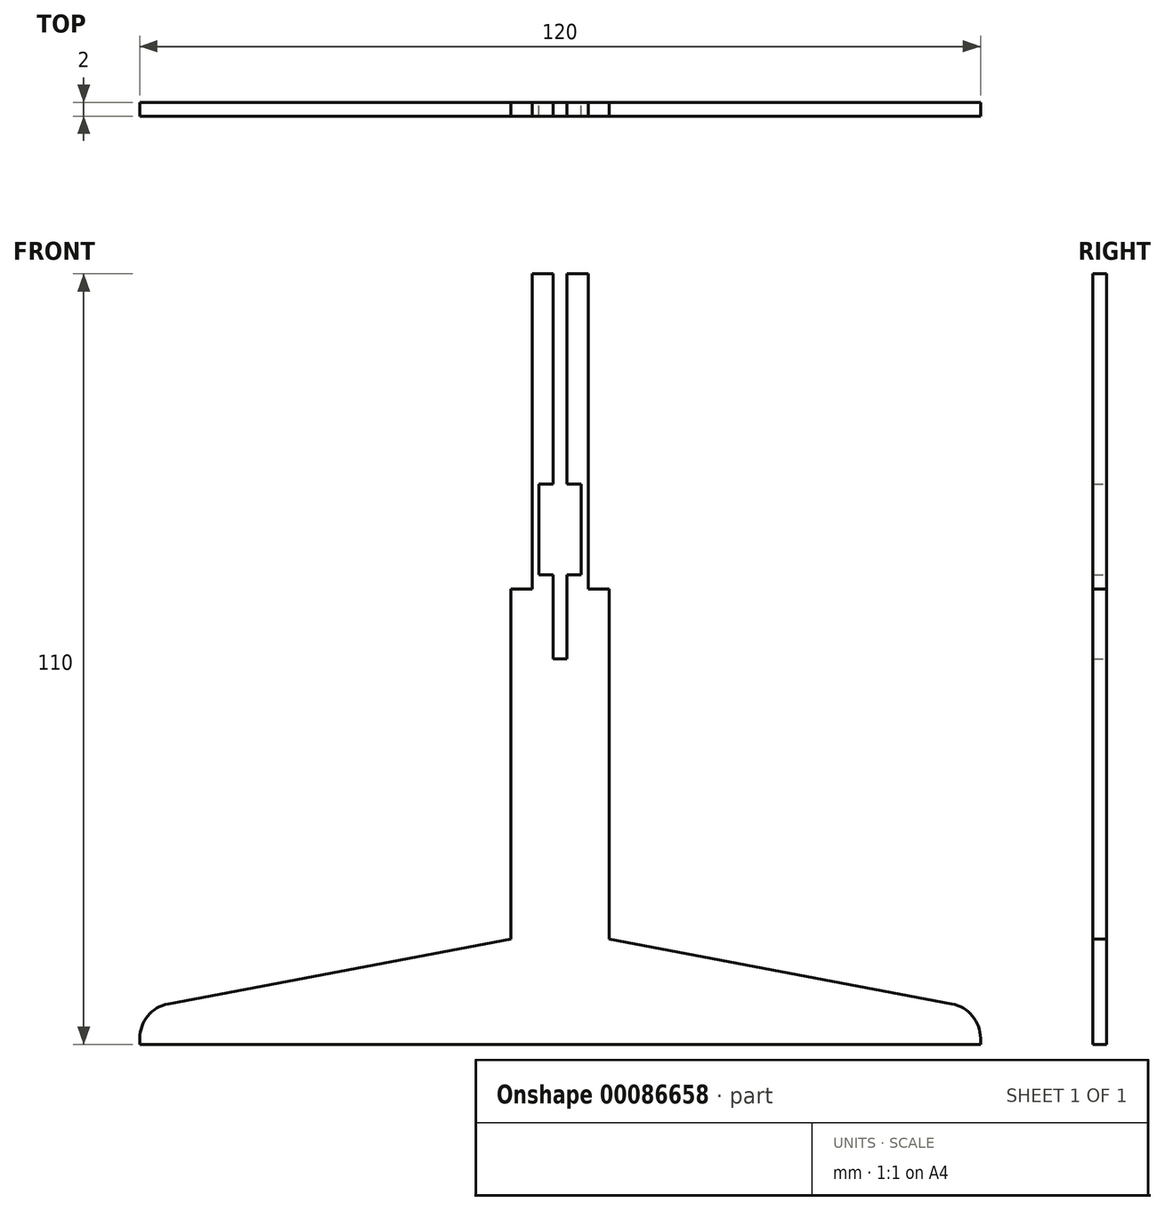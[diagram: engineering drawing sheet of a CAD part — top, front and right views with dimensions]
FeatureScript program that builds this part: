
annotation { "Feature Type Name" : "Feature", "Feature Type Description" : "" }
export const myFeature = defineFeature(function(context is Context, id is Id, definition is map)
    precondition{}
    {
        {
            var Q0;
            Q0=qCreatedBy(makeId("Front.planeOp"),FACE);
            var sketch = newSketch(context, id + "F0", { "sketchPlane" : qUnion([Q0])});
            skLineSegment(sketch, "E0", {"start": v(-1, 55) * mm, "end": v(1, 55) * mm});
            skLineSegment(sketch, "E1", {"start": v(1, 55) * mm, "end": v(1, 67) * mm});
            skLineSegment(sketch, "E2", {"start": v(1, 110) * mm, "end": v(4, 110) * mm});
            skLineSegment(sketch, "E3", {"start": v(4, 110) * mm, "end": v(4, 65) * mm});
            skLineSegment(sketch, "E4", {"start": v(4, 65) * mm, "end": v(7, 65) * mm});
            skLineSegment(sketch, "E5", {"start": v(7, 65) * mm, "end": v(7, 15) * mm});
            skLineSegment(sketch, "E6", {"start": v(60, 0) * mm, "end": v(-60, 0) * mm});
            skLineSegment(sketch, "E7", {"start": v(-7, 15) * mm, "end": v(-7, 65) * mm});
            skLineSegment(sketch, "E8", {"start": v(-7, 65) * mm, "end": v(-4, 65) * mm});
            skLineSegment(sketch, "E9", {"start": v(-4, 65) * mm, "end": v(-4, 110) * mm});
            skLineSegment(sketch, "E10", {"start": v(-4, 110) * mm, "end": v(-1, 110) * mm});
            skLineSegment(sketch, "E11", {"start": v(-1, 110) * mm, "end": v(-1, 80) * mm});
            skLineSegment(sketch, "E12", {"start": v(-1, 80) * mm, "end": v(-3, 80) * mm});
            skLineSegment(sketch, "E13", {"start": v(-3, 80) * mm, "end": v(-3, 67) * mm});
            skLineSegment(sketch, "E14", {"start": v(-3, 67) * mm, "end": v(-1, 67) * mm});
            skLineSegment(sketch, "E15", {"start": v(-1, 67) * mm, "end": v(-1, 55) * mm});
            skLineSegment(sketch, "E16", {"start": v(1, 67) * mm, "end": v(3, 67) * mm});
            skLineSegment(sketch, "E17", {"start": v(3, 67) * mm, "end": v(3, 80) * mm});
            skLineSegment(sketch, "E18", {"start": v(3, 80) * mm, "end": v(1, 80) * mm});
            skLineSegment(sketch, "E19", {"start": v(1, 80) * mm, "end": v(1, 110) * mm});
            skLineSegment(sketch, "E20", {"start": v(7, 15) * mm, "end": v(60, 5) * mm});
            skLineSegment(sketch, "E21", {"start": v(60, 5) * mm, "end": v(60, 0) * mm});
            skLineSegment(sketch, "E22", {"start": v(-7, 15) * mm, "end": v(-60, 5) * mm});
            skLineSegment(sketch, "E23", {"start": v(-60, 5) * mm, "end": v(-60, 0) * mm});
            skSolve(sketch);
        }
        {
            var Q0;
            Q0=makeQuery(id+"F0.imprint","IMPRINT",FACE,{"disambiguationData":[TD([[makeQuery(id+"F0.imprint","IMPRINT",EDGE,{"derivedFrom":sQuery(id+"F0.wireOp",EDGE,"E0")}),-1.0]])]});
            extrude(context, id + "F1", {"entities" : qUnion([Q0]), "depth" : 1 * mm, "hasSecondDirection" : true, "secondDirectionOppositeDirection" : true, "secondDirectionDepth" : 1 * mm});
        }
        {
            var Q0;
            Q0=makeQuery(id+"F1.opExtrude","SWEPT_EDGE",EDGE,{"disambiguationData":[OSD([sQuery(id+"F0.wireOp",EDGE,"E22"),sQuery(id+"F0.wireOp",EDGE,"E23")])]});
            var Q1;
            Q1=makeQuery(id+"F1.opExtrude","SWEPT_EDGE",EDGE,{"disambiguationData":[OSD([sQuery(id+"F0.wireOp",EDGE,"E20"),sQuery(id+"F0.wireOp",EDGE,"E21")])]});
            fillet(context, id + "F2", {"entities" : qUnion([Q0, Q1]), "radius" : 5 * mm, "tangentPropagation" : true, "allowEdgeOverflow" : false});
        }
    });
